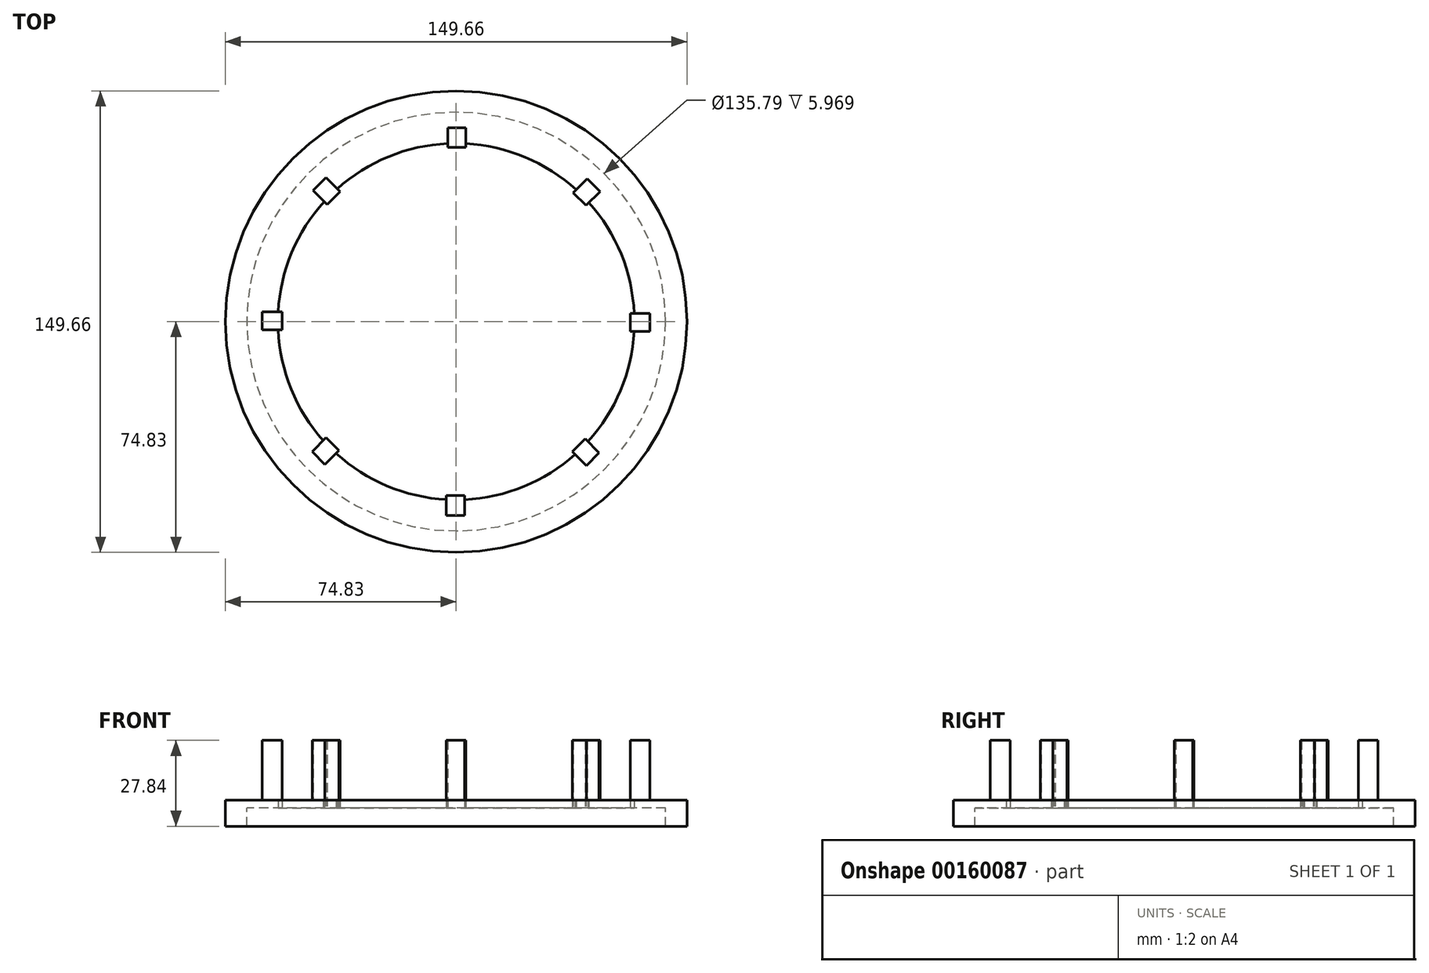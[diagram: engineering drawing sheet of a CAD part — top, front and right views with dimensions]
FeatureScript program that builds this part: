
annotation { "Feature Type Name" : "Feature", "Feature Type Description" : "" }
export const myFeature = defineFeature(function(context is Context, id is Id, definition is map)
    precondition{}
    {
        {
            var Q0;
            Q0=qCreatedBy(makeId("Top.planeOp"),FACE);
            var sketch = newSketch(context, id + "F0", { "sketchPlane" : qUnion([Q0])});
            skCircle(sketch, "E0", {"center": v(0, 0) * mm, "radius": 67.9 * mm});
            skCircle(sketch, "E1", {"center": v(0, 0) * mm, "radius": 74.83 * mm});
            skSolve(sketch);
        }
        {
            var Q0;
            Q0 = qSketchRegion(id + "F0", true);
            extrude(context, id + "F1", {"entities" : qUnion([Q0]), "oppositeDirection" : true, "depth" : 5.97 * mm});
        }
        {
            var Q0;
            Q0=qCreatedBy(makeId("Top.planeOp"),FACE);
            var sketch = newSketch(context, id + "F2", { "sketchPlane" : qUnion([Q0])});
            skCircle(sketch, "E2", {"center": v(0, 0) * mm, "radius": 74.83 * mm});
            skCircle(sketch, "E3", {"center": v(0, 0) * mm, "radius": 57.81 * mm});
            skSolve(sketch);
        }
        {
            var Q0;
            Q0 = qSketchRegion(id + "F2", true);
            extrude(context, id + "F3", {"entities" : qUnion([Q0]), "operationType" : NewBodyOperationType.ADD, "depth" : 2.54 * mm});
        }
        {
            var Q0;
            Q0=qCreatedBy(makeId("Top.planeOp"),FACE);
            var sketch = newSketch(context, id + "F4", { "sketchPlane" : qUnion([Q0])});
            skLineSegment(sketch, "E4.bottom", {"start": v(-62.87, 3.17) * mm, "end": v(-56.44, 3.17) * mm});
            skLineSegment(sketch, "E4.top", {"start": v(-62.87, -2.71) * mm, "end": v(-56.44, -2.71) * mm});
            skLineSegment(sketch, "E4.left", {"start": v(-62.87, 3.17) * mm, "end": v(-62.87, -2.71) * mm});
            skLineSegment(sketch, "E4.right", {"start": v(-56.44, 3.17) * mm, "end": v(-56.44, -2.71) * mm});
            skLineSegment(sketch, "E5.1.0", {"start": v(-46.7, -42.2) * mm, "end": v(-42.16, -37.67) * mm});
            skLineSegment(sketch, "E5.1.1", {"start": v(-46.7, -42.2) * mm, "end": v(-42.53, -46.37) * mm});
            skLineSegment(sketch, "E5.1.2", {"start": v(-42.53, -46.37) * mm, "end": v(-38, -41.83) * mm});
            skLineSegment(sketch, "E5.1.3", {"start": v(-42.16, -37.67) * mm, "end": v(-38, -41.83) * mm});
            skLineSegment(sketch, "E5.2.0", {"start": v(-3.17, -62.87) * mm, "end": v(-3.17, -56.44) * mm});
            skLineSegment(sketch, "E5.2.1", {"start": v(-3.17, -62.87) * mm, "end": v(2.71, -62.87) * mm});
            skLineSegment(sketch, "E5.2.2", {"start": v(2.71, -62.87) * mm, "end": v(2.71, -56.44) * mm});
            skLineSegment(sketch, "E5.2.3", {"start": v(-3.17, -56.44) * mm, "end": v(2.71, -56.44) * mm});
            skLineSegment(sketch, "E5.3.0", {"start": v(42.2, -46.7) * mm, "end": v(37.67, -42.16) * mm});
            skLineSegment(sketch, "E5.3.1", {"start": v(42.2, -46.7) * mm, "end": v(46.37, -42.53) * mm});
            skLineSegment(sketch, "E5.3.2", {"start": v(46.37, -42.53) * mm, "end": v(41.83, -38) * mm});
            skLineSegment(sketch, "E5.3.3", {"start": v(37.67, -42.16) * mm, "end": v(41.83, -38) * mm});
            skLineSegment(sketch, "E5.4.0", {"start": v(62.87, -3.17) * mm, "end": v(56.44, -3.17) * mm});
            skLineSegment(sketch, "E5.4.1", {"start": v(62.87, -3.17) * mm, "end": v(62.87, 2.71) * mm});
            skLineSegment(sketch, "E5.4.2", {"start": v(62.87, 2.71) * mm, "end": v(56.44, 2.71) * mm});
            skLineSegment(sketch, "E5.4.3", {"start": v(56.44, -3.17) * mm, "end": v(56.44, 2.71) * mm});
            skLineSegment(sketch, "E5.5.0", {"start": v(46.7, 42.2) * mm, "end": v(42.16, 37.67) * mm});
            skLineSegment(sketch, "E5.5.1", {"start": v(46.7, 42.2) * mm, "end": v(42.53, 46.37) * mm});
            skLineSegment(sketch, "E5.5.2", {"start": v(42.53, 46.37) * mm, "end": v(38, 41.83) * mm});
            skLineSegment(sketch, "E5.5.3", {"start": v(42.16, 37.67) * mm, "end": v(38, 41.83) * mm});
            skLineSegment(sketch, "E5.6.0", {"start": v(3.17, 62.87) * mm, "end": v(3.17, 56.44) * mm});
            skLineSegment(sketch, "E5.6.1", {"start": v(3.17, 62.87) * mm, "end": v(-2.71, 62.87) * mm});
            skLineSegment(sketch, "E5.6.2", {"start": v(-2.71, 62.87) * mm, "end": v(-2.71, 56.44) * mm});
            skLineSegment(sketch, "E5.6.3", {"start": v(3.17, 56.44) * mm, "end": v(-2.71, 56.44) * mm});
            skLineSegment(sketch, "E5.7.0", {"start": v(-42.2, 46.7) * mm, "end": v(-37.67, 42.16) * mm});
            skLineSegment(sketch, "E5.7.1", {"start": v(-42.2, 46.7) * mm, "end": v(-46.37, 42.53) * mm});
            skLineSegment(sketch, "E5.7.2", {"start": v(-46.37, 42.53) * mm, "end": v(-41.83, 38) * mm});
            skLineSegment(sketch, "E5.7.3", {"start": v(-37.67, 42.16) * mm, "end": v(-41.83, 38) * mm});
            skPoint(sketch, "E5.center", {"position": v(0, 0) * mm});
            skSolve(sketch);
        }
        {
            var Q0;
            Q0 = qSketchRegion(id + "F4", true);
            extrude(context, id + "F5", {"entities" : qUnion([Q0]), "operationType" : NewBodyOperationType.ADD, "depth" : 21.87 * mm});
        }
    });
